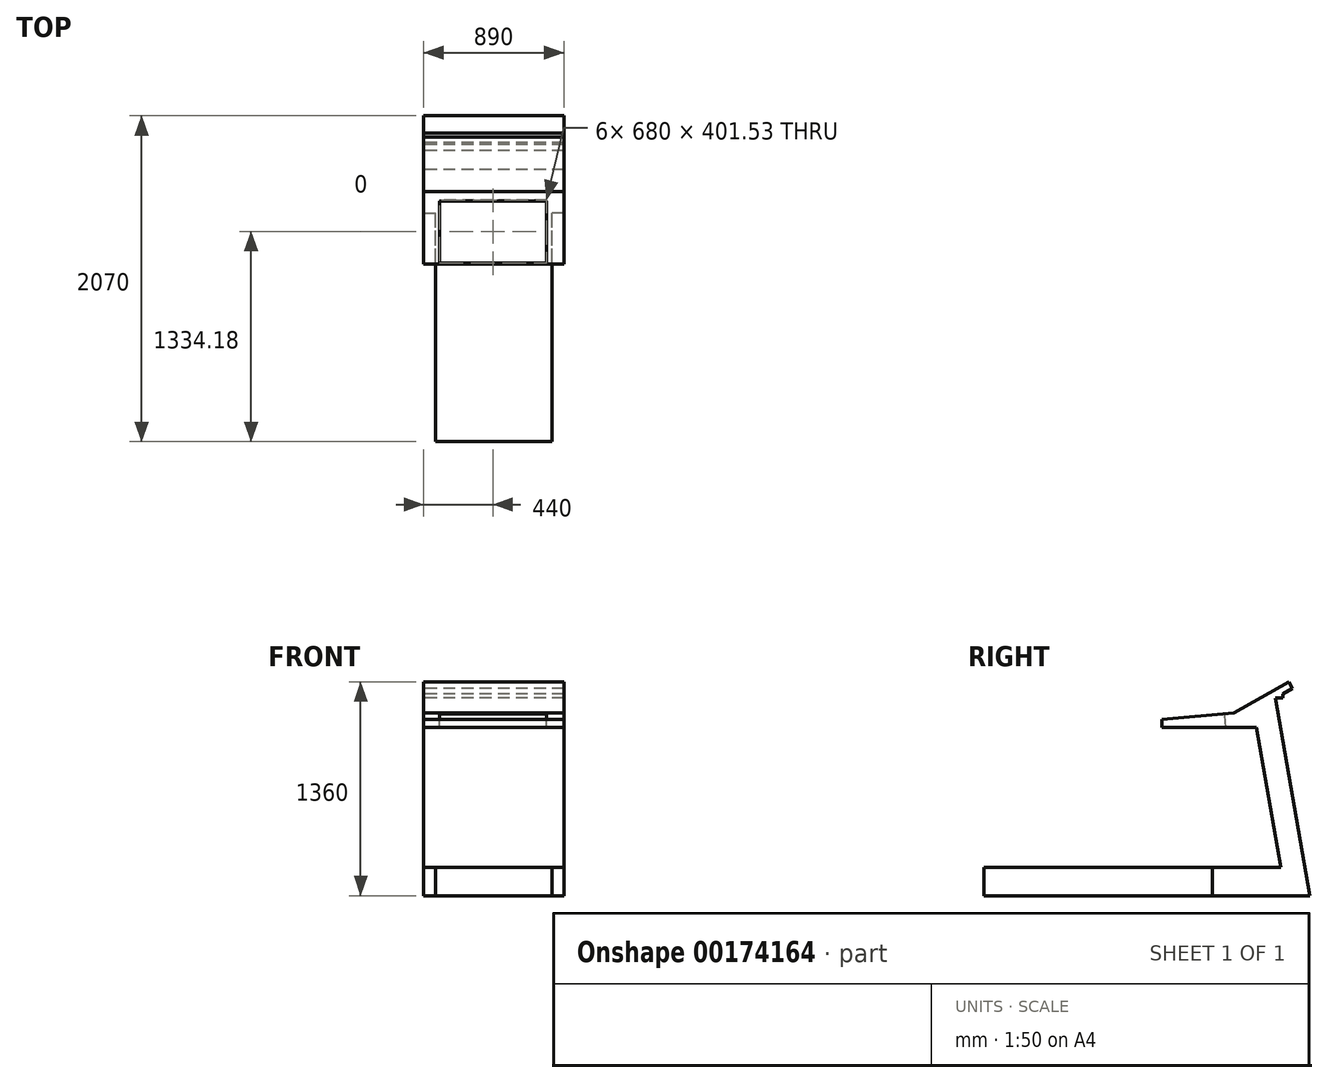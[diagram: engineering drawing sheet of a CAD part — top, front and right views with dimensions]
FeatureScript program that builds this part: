
annotation { "Feature Type Name" : "Feature", "Feature Type Description" : "" }
export const myFeature = defineFeature(function(context is Context, id is Id, definition is map)
    precondition{}
    {
        {
            var Q0;
            Q0=qCreatedBy(makeId("Right.planeOp"),FACE);
            var sketch = newSketch(context, id + "F0", { "sketchPlane" : qUnion([Q0])});
            skLineSegment(sketch, "E0", {"start": v(0, 0) * mm, "end": v(2070, 0) * mm});
            skLineSegment(sketch, "E1", {"start": v(2070, 0) * mm, "end": v(1848.46, 1256.44) * mm});
            skLineSegment(sketch, "E2", {"start": v(1848.46, 1256.44) * mm, "end": v(1898.45, 1256.7) * mm});
            skLineSegment(sketch, "E3", {"start": v(1898.45, 1256.7) * mm, "end": v(1898.45, 1281.7) * mm});
            skLineSegment(sketch, "E4", {"start": v(1898.45, 1281.7) * mm, "end": v(1959.08, 1316.7) * mm});
            skLineSegment(sketch, "E5", {"start": v(1959.08, 1316.7) * mm, "end": v(1934.08, 1360) * mm});
            skLineSegment(sketch, "E6", {"start": v(1934.08, 1360) * mm, "end": v(1587.67, 1160) * mm});
            skLineSegment(sketch, "E7", {"start": v(1587.67, 1160) * mm, "end": v(1129.04, 1119.88) * mm});
            skLineSegment(sketch, "E8", {"start": v(1129.04, 1119.88) * mm, "end": v(1129.04, 1069.88) * mm});
            skLineSegment(sketch, "E9", {"start": v(1129.04, 1069.88) * mm, "end": v(1729.04, 1069.88) * mm});
            skLineSegment(sketch, "E10", {"start": v(1729.04, 1069.88) * mm, "end": v(1885.95, 180) * mm});
            skLineSegment(sketch, "E11", {"start": v(1885.95, 180) * mm, "end": v(0, 180) * mm});
            skLineSegment(sketch, "E12", {"start": v(0, 180) * mm, "end": v(0, 0) * mm});
            skSolve(sketch);
        }
        {
            var Q0;
            Q0=qSketchRegion(id+"F0",true);
            extrude(context, id + "F1", {"entities" : qUnion([Q0]), "endBound" : BoundingType.SYMMETRIC, "depth" : 890 * mm});
        }
        {
            var Q0;
            Q0=makeQuery(id+"F1.opExtrude","SWEPT_FACE",FACE,{"disambiguationData":[OSD([sQuery(id+"F0.wireOp",EDGE,"E7")])]});
            var sketch = newSketch(context, id + "F2", { "sketchPlane" : qUnion([Q0])});
            skLineSegment(sketch, "E13.bottom", {"start": v(-345, 1222.35) * mm, "end": v(335, 1222.35) * mm});
            skLineSegment(sketch, "E13.top", {"start": v(-345, 1622.35) * mm, "end": v(335, 1622.35) * mm});
            skLineSegment(sketch, "E13.left", {"start": v(-345, 1222.35) * mm, "end": v(-345, 1622.35) * mm});
            skLineSegment(sketch, "E13.right", {"start": v(335, 1222.35) * mm, "end": v(335, 1622.35) * mm});
            skSolve(sketch);
        }
        {
            var Q0;
            Q0=makeQuery(id+"F2.imprint","IMPRINT",FACE,{"disambiguationData":[TD([[makeQuery(id+"F2.imprint","IMPRINT",EDGE,{"derivedFrom":sQuery(id+"F2.wireOp",EDGE,"E13.bottom")}),-1.0]])]});
            var Q1;
            Q1=makeQuery(id+"F1.opExtrude","SWEPT_FACE",FACE,{"disambiguationData":[OSD([sQuery(id+"F0.wireOp",EDGE,"E9")])]});
            extrude(context, id + "F3", {"entities" : qUnion([Q0]), "operationType" : NewBodyOperationType.REMOVE, "endBound" : BoundingType.UP_TO_SURFACE, "oppositeDirection" : true, "endBoundEntityFace" : qUnion([Q1]), "depth" : 25 * mm});
        }
        {
            var Q0;
            Q0=makeQuery(id+"F1.opExtrude","SWEPT_FACE",FACE,{"disambiguationData":[OSD([sQuery(id+"F0.wireOp",EDGE,"E11")])]});
            var sketch = newSketch(context, id + "F4", { "sketchPlane" : qUnion([Q0])});
            skLineSegment(sketch, "E14.bottom", {"start": v(-445, 0) * mm, "end": v(-370, 0) * mm});
            skLineSegment(sketch, "E14.top", {"start": v(-445, 1450) * mm, "end": v(-370, 1450) * mm});
            skLineSegment(sketch, "E14.left", {"start": v(-445, 0) * mm, "end": v(-445, 1450) * mm});
            skLineSegment(sketch, "E14.right", {"start": v(-370, 0) * mm, "end": v(-370, 1450) * mm});
            skLineSegment(sketch, "E15", {"start": v(0, 0) * mm, "end": v(0, 1005.63) * mm, "construction": true});
            skPoint(sketch, "E15.endSnap0", {"position": v(0, 0) * mm});
            skLineSegment(sketch, "E16.MirrorCS", {"start": v(370, 0) * mm, "end": v(370, 1450) * mm});
            skLineSegment(sketch, "E17.MirrorCS", {"start": v(445, 1450) * mm, "end": v(370, 1450) * mm});
            skLineSegment(sketch, "E18.MirrorCS", {"start": v(445, 0) * mm, "end": v(370, 0) * mm});
            skLineSegment(sketch, "E19.MirrorCS", {"start": v(445, 0) * mm, "end": v(445, 1450) * mm});
            skSolve(sketch);
        }
        {
            var Q0;
            Q0=makeQuery(id+"F4.imprint","IMPRINT",FACE,{"disambiguationData":[TD([[makeQuery(id+"F4.imprint","IMPRINT",EDGE,{"derivedFrom":sQuery(id+"F4.wireOp",EDGE,"E14.bottom")}),-1.0]])]});
            var Q1;
            Q1=makeQuery(id+"F4.imprint","IMPRINT",FACE,{"disambiguationData":[TD([[makeQuery(id+"F4.imprint","IMPRINT",EDGE,{"derivedFrom":sQuery(id+"F4.wireOp",EDGE,"E16.MirrorCS")}),-1.0]])]});
            extrude(context, id + "F5", {"entities" : qUnion([Q0, Q1]), "operationType" : NewBodyOperationType.REMOVE, "endBound" : BoundingType.THROUGH_ALL, "oppositeDirection" : true, "depth" : 25 * mm});
        }
    });
